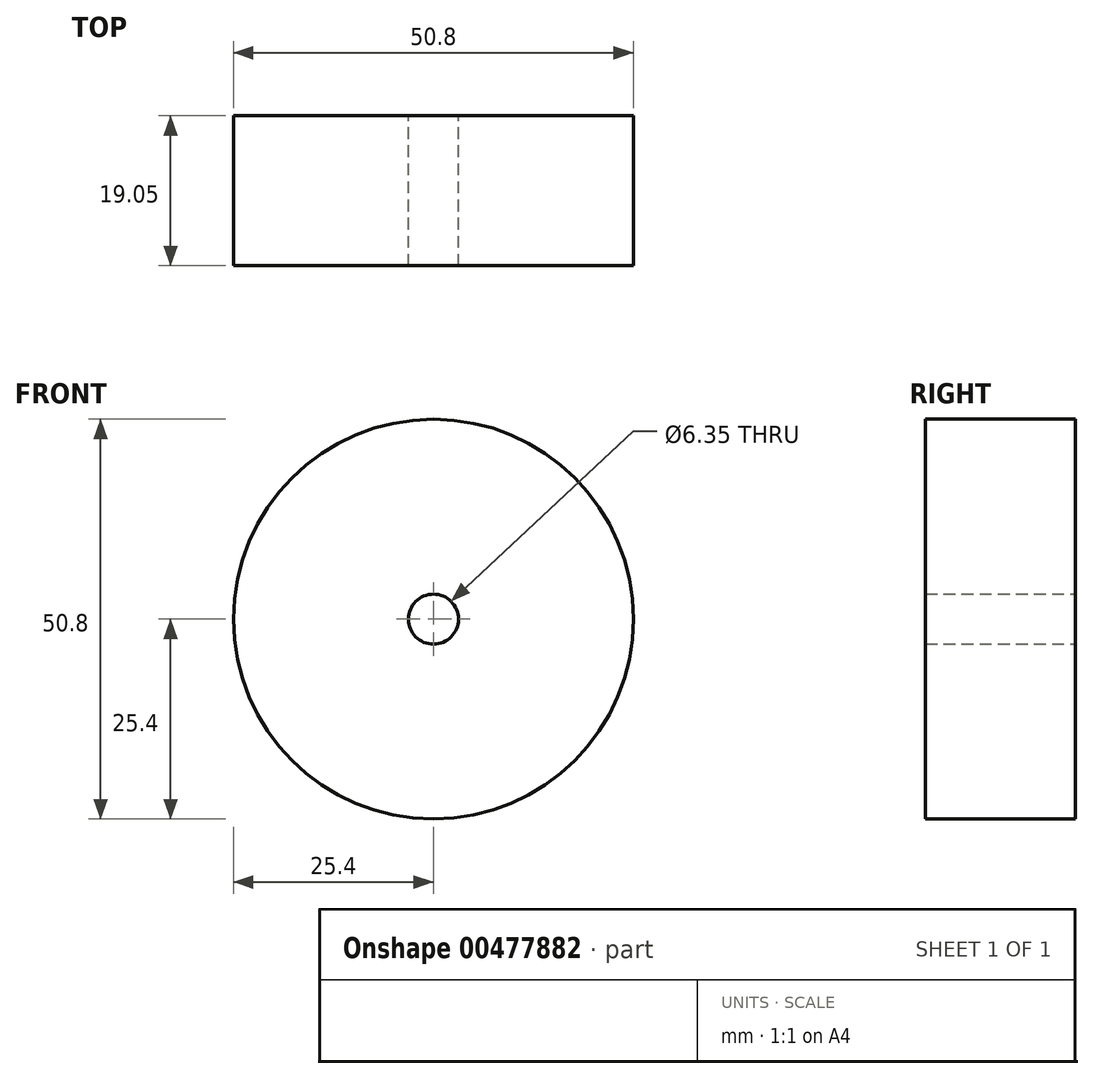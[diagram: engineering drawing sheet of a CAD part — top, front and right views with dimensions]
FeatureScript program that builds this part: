
annotation { "Feature Type Name" : "Feature", "Feature Type Description" : "" }
export const myFeature = defineFeature(function(context is Context, id is Id, definition is map)
    precondition{}
    {
        {
            var Q0;
            Q0=qCreatedBy(makeId("Front.planeOp"),FACE);
            var sketch = newSketch(context, id + "F0", { "sketchPlane" : qUnion([Q0])});
            skCircle(sketch, "E0", {"center": v(0, 0) * mm, "radius": 25.4 * mm});
            skSolve(sketch);
        }
        {
            var Q0;
            Q0=makeQuery(id+"F0.imprint","IMPRINT",FACE,{"disambiguationData":[TD([[makeQuery(id+"F0.imprint","IMPRINT",EDGE,{"derivedFrom":sQuery(id+"F0.wireOp",EDGE,"E0")}),1.0]])]});
            extrude(context, id + "F1", {"entities" : qUnion([Q0]), "depth" : 19.05 * mm, "offsetDistance" : 25.4 * mm});
        }
        {
            var Q0;
            Q0=sQuery(id+"F0.wireOp",VERTEX,"E0.center");
            var Q1;
            Q1=makeQuery(id+"F1.opExtrude","SWEPT_BODY",BODY,{"disambiguationData":[OSD([sQuery(id+"F0.wireOp",EDGE,"E0")])]});
            hole(context, id + "F2", {"style" : HoleStyle.SIMPLE, "endStyle" : HoleEndStyle.THROUGH, "oppositeDirection" : true, "holeDiameter" : 6.35 * mm, "majorDiameter" : 6.35 * mm, "tappedDepth" : 12.7 * mm, "tapClearance" : 3, "locations" : qUnion([Q0]), "scope" : qUnion([Q1])});
        }
    });
